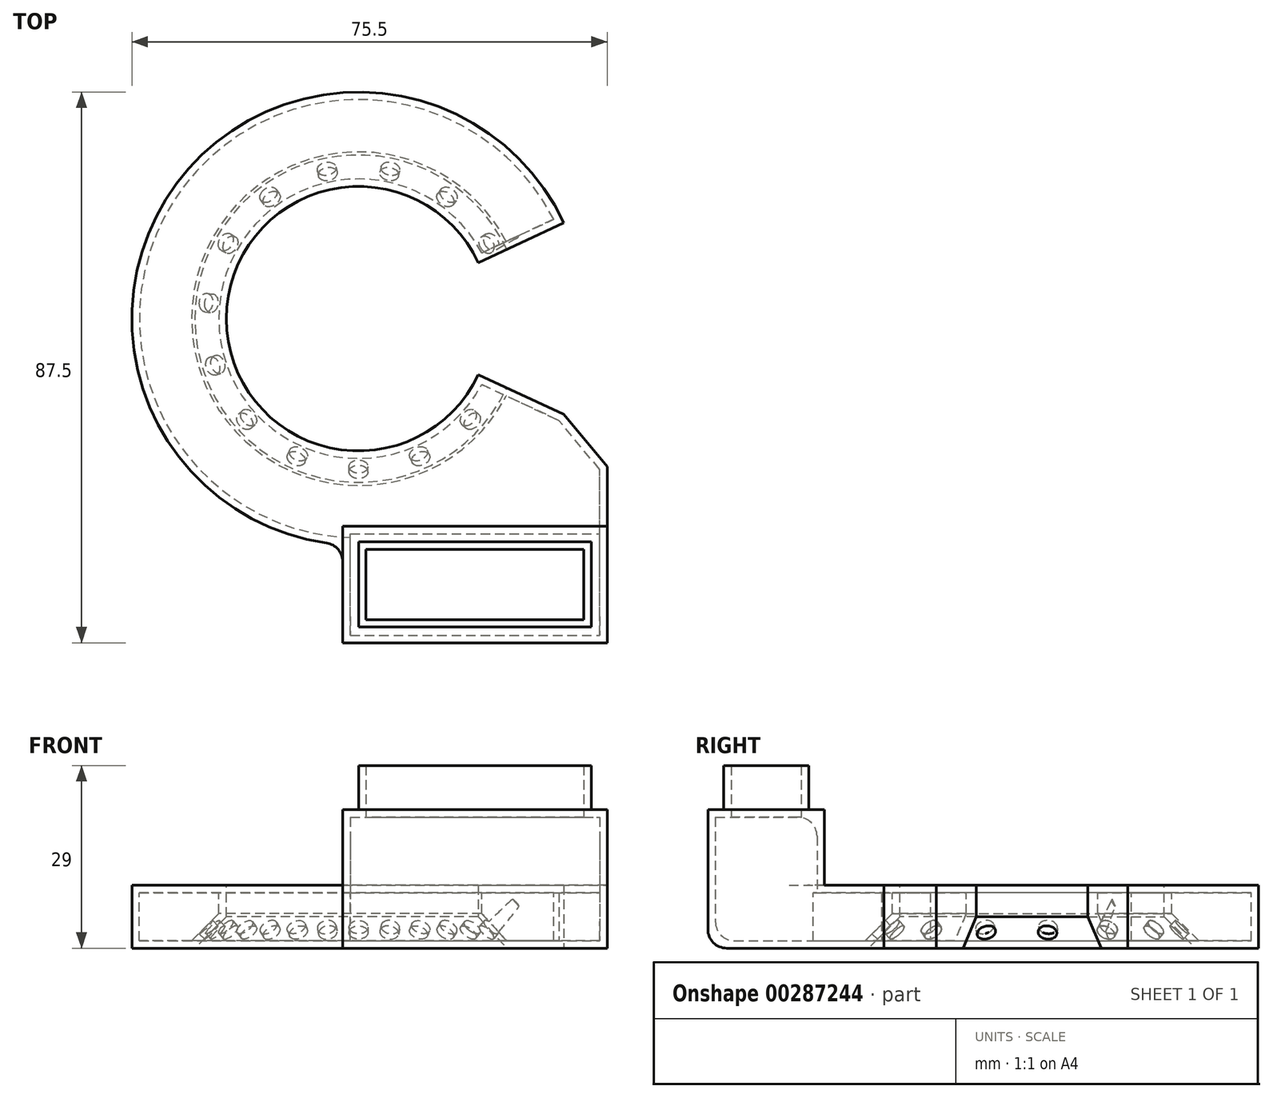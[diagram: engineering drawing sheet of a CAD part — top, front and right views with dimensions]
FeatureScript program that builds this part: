
annotation { "Feature Type Name" : "Feature", "Feature Type Description" : "" }
export const myFeature = defineFeature(function(context is Context, id is Id, definition is map)
    precondition{}
    {
        {
            var Q0;
            Q0=qCreatedBy(makeId("Front.planeOp"),FACE);
            var sketch = newSketch(context, id + "F0", { "sketchPlane" : qUnion([Q0])});
            skLineSegment(sketch, "E0", {"start": v(0, 66.2) * mm, "end": v(0, -56.66) * mm, "construction": true});
            skLineSegment(sketch, "E1", {"start": v(21, 10) * mm, "end": v(36, 10) * mm});
            skLineSegment(sketch, "E2", {"start": v(36, 10) * mm, "end": v(36, 0) * mm});
            skLineSegment(sketch, "E3", {"start": v(36, 0) * mm, "end": v(26, 0) * mm});
            skLineSegment(sketch, "E4", {"start": v(21, 10) * mm, "end": v(21, 5) * mm});
            skLineSegment(sketch, "E5", {"start": v(21, 5) * mm, "end": v(26, 0) * mm});
            skSolve(sketch);
        }
        {
            var Q0;
            Q0=makeQuery(id+"F0.imprint","IMPRINT",FACE,{"disambiguationData":[TD([[makeQuery(id+"F0.imprint","IMPRINT",EDGE,{"derivedFrom":sQuery(id+"F0.wireOp",EDGE,"E1")}),-1.0]])]});
            var Q1;
            Q1=sQuery(id+"F0.wireOp",EDGE,"E0");
            revolve(context, id + "F1", {"entities" : qUnion([Q0]), "axis" : qUnion([Q1]), "revolveType" : RevolveType.TWO_DIRECTIONS, "angle" : 335 * degree, "angleBack" : 25 * degree});
        }
        {
            var Q0;
            Q0=qCreatedBy(makeId("Top.planeOp"),FACE);
            var sketch = newSketch(context, id + "F2", { "sketchPlane" : qUnion([Q0])});
            skLineSegment(sketch, "E6.bottom", {"start": v(-2.5, -51.5) * mm, "end": v(39.5, -51.5) * mm});
            skLineSegment(sketch, "E6.left", {"start": v(-2.5, -51.5) * mm, "end": v(-2.5, -31.44) * mm});
            skLineSegment(sketch, "E6.right", {"start": v(39.5, -51.5) * mm, "end": v(39.5, -23.5) * mm});
            skPoint(sketch, "E7.orphan", {"position": v(23.56, -10.99) * mm});
            skPoint(sketch, "E8.orphan", {"position": v(23.56, 10.99) * mm});
            skPoint(sketch, "E9.0", {"position": v(32.63, -15.21) * mm});
            skLineSegment(sketch, "E10", {"start": v(39.5, -23.5) * mm, "end": v(32.63, -15.21) * mm});
            skLineSegment(sketch, "E11", {"start": v(32.63, -15.21) * mm, "end": v(-2.5, -31.44) * mm});
            skSolve(sketch);
        }
        {
            var Q0;
            Q0=makeQuery(id+"F2.imprint","IMPRINT",FACE,{"disambiguationData":[TD([[makeQuery(id+"F2.imprint","IMPRINT",EDGE,{"derivedFrom":sQuery(id+"F2.wireOp",EDGE,"E6.bottom")}),1.0]])]});
            var Q1;
            Q1=makeQuery(id+"F1.opRevolve","SWEPT_FACE",FACE,{"disambiguationData":[OSD([sQuery(id+"F0.wireOp",EDGE,"E1")])]});
            extrude(context, id + "F3", {"entities" : qUnion([Q0]), "operationType" : NewBodyOperationType.ADD, "endBound" : BoundingType.UP_TO_SURFACE, "endBoundEntityFace" : qUnion([Q1]), "depth" : 25 * mm});
        }
        {
            var Q0;
            Q0=makeQuery(id+"F3.boolean.opBoolean","MERGE",FACE,{"derivedFrom":[makeQuery(id+"F1.opRevolve","SWEPT_FACE",FACE,{"disambiguationData":[OSD([sQuery(id+"F0.wireOp",EDGE,"E1")])]}),makeQuery(id+"F3.opExtrude","CAP_FACE",FACE,{"disambiguationData":[OSD([sQuery(id+"F2.wireOp",EDGE,"E6.bottom"),sQuery(id+"F2.wireOp",EDGE,"E6.left"),sQuery(id+"F2.wireOp",EDGE,"E6.right"),sQuery(id+"F2.wireOp",EDGE,"E10"),sQuery(id+"F2.wireOp",EDGE,"E11")])],"isStart":false})]});
            var sketch = newSketch(context, id + "F4", { "sketchPlane" : qUnion([Q0])});
            skPoint(sketch, "E12.0", {"position": v(-2.5, -51.5) * mm});
            skLineSegment(sketch, "E13.bottom", {"start": v(-2.5, -51.5) * mm, "end": v(39.5, -51.5) * mm});
            skLineSegment(sketch, "E13.top", {"start": v(-2.5, -32.96) * mm, "end": v(39.5, -32.96) * mm});
            skLineSegment(sketch, "E13.left", {"start": v(-2.5, -51.5) * mm, "end": v(-2.5, -32.96) * mm});
            skLineSegment(sketch, "E13.right", {"start": v(39.5, -51.5) * mm, "end": v(39.5, -32.96) * mm});
            skSolve(sketch);
        }
        {
            var Q0;
            Q0=makeQuery(id+"F4.imprint","IMPRINT",FACE,{"disambiguationData":[TD([[makeQuery(id+"F4.imprint","IMPRINT",EDGE,{"derivedFrom":sQuery(id+"F4.wireOp",EDGE,"E13.bottom")}),1.0]])]});
            extrude(context, id + "F5", {"entities" : qUnion([Q0]), "operationType" : NewBodyOperationType.ADD, "depth" : 12 * mm});
        }
        {
            var Q0;
            Q0=makeQuery(id+"F5.opExtrude","CAP_FACE",FACE,{"disambiguationData":[OSD([sQuery(id+"F4.wireOp",EDGE,"E13.bottom"),sQuery(id+"F4.wireOp",EDGE,"E13.top"),sQuery(id+"F4.wireOp",EDGE,"E13.left"),sQuery(id+"F4.wireOp",EDGE,"E13.right")])],"isStart":false});
            var sketch = newSketch(context, id + "F6", { "sketchPlane" : qUnion([Q0])});
            skPoint(sketch, "E14.0", {"position": v(-2.5, -32.96) * mm});
            skPoint(sketch, "E15.0", {"position": v(-2.5, -51.5) * mm});
            skPoint(sketch, "E16.0", {"position": v(39.5, -51.5) * mm});
            skPoint(sketch, "E17.0", {"position": v(39.5, -32.96) * mm});
            skLineSegment(sketch, "E18", {"start": v(-2.5, -32.96) * mm, "end": v(39.5, -51.5) * mm, "construction": true});
            skLineSegment(sketch, "E19", {"start": v(-2.5, -51.5) * mm, "end": v(39.5, -32.96) * mm, "construction": true});
            skLineSegment(sketch, "E20.bottom", {"start": v(37, -35.46) * mm, "end": v(0, -35.46) * mm});
            skLineSegment(sketch, "E20.top", {"start": v(37, -49) * mm, "end": v(0, -49) * mm});
            skLineSegment(sketch, "E20.left", {"start": v(37, -35.46) * mm, "end": v(37, -49) * mm});
            skLineSegment(sketch, "E20.right", {"start": v(0, -35.46) * mm, "end": v(0, -49) * mm});
            skPoint(sketch, "E20.middle", {"position": v(18.5, -42.23) * mm});
            skSolve(sketch);
        }
        {
            var Q0;
            Q0=makeQuery(id+"F6.imprint","IMPRINT",FACE,{"disambiguationData":[TD([[makeQuery(id+"F6.imprint","IMPRINT",EDGE,{"derivedFrom":sQuery(id+"F6.wireOp",EDGE,"E20.bottom")}),1.0]])]});
            extrude(context, id + "F7", {"entities" : qUnion([Q0]), "operationType" : NewBodyOperationType.ADD, "depth" : 7 * mm});
        }
        {
            var Q0;
            Q0=makeQuery(id+"F7.opExtrude","CAP_FACE",FACE,{"disambiguationData":[OSD([sQuery(id+"F6.wireOp",EDGE,"E20.bottom"),sQuery(id+"F6.wireOp",EDGE,"E20.top"),sQuery(id+"F6.wireOp",EDGE,"E20.left"),sQuery(id+"F6.wireOp",EDGE,"E20.right")])],"isStart":false});
            shell(context, id + "F8", {"entities" : qUnion([Q0]), "thickness" : 1.2 * mm});
        }
        {
            var Q0;
            Q0=qCreatedBy(makeId("Top.planeOp"),FACE);
            var sketch = newSketch(context, id + "F9", { "sketchPlane" : qUnion([Q0])});
            skLineSegment(sketch, "E21", {"start": v(71.7, 0) * mm, "end": v(-68.59, 0) * mm});
            skSolve(sketch);
        }
        {
            var Q0;
            Q0=sQuery(id+"F9.wireOp",EDGE,"E21");
            cPlane(context, id + "F10", {"entities" : qUnion([Q0]), "cplaneType" : CPlaneType.LINE_ANGLE, "offset" : 25 * mm, "angle" : 45 * degree, "width" : 150 * mm, "height" : 150 * mm});
        }
        {
            var Q0;
            Q0=qCreatedBy(id+"F10.planeOp",FACE);
            var sketch = newSketch(context, id + "F11", { "sketchPlane" : qUnion([Q0])});
            skCircle(sketch, "E22", {"center": v(0, -14.85) * mm, "radius": 1.5 * mm});
            skSolve(sketch);
        }
        {
            var Q0;
            Q0=makeQuery(id+"F11.imprint","IMPRINT",FACE,{"disambiguationData":[TD([[makeQuery(id+"F11.imprint","IMPRINT",EDGE,{"derivedFrom":sQuery(id+"F11.wireOp",EDGE,"E22")}),1.0]])]});
            extrude(context, id + "F12", {"entities" : qUnion([Q0]), "depth" : 25 * mm});
        }
        {
            var Q0;
            Q0=makeQuery(id+"F12.opExtrude","SWEPT_BODY",BODY,{"disambiguationData":[OSD([sQuery(id+"F11.wireOp",EDGE,"E22")])]});
            var Q1;
            Q1=sQuery(id+"F0.wireOp",EDGE,"E0");
            circularPattern(context, id + "F13", {"operationType" : NewBodyOperationType.REMOVE, "entities" : qUnion([Q0]), "axis" : qUnion([Q1]), "angle" : 360 * degree, "instanceCount" : 15, "equalSpace" : true});
        }
        {
            var Q0;
            Q0=makeQuery(id+"F3.opExtrude","CAP_EDGE",EDGE,{"disambiguationData":[OSD([sQuery(id+"F2.wireOp",EDGE,"E6.bottom")])],"isStart":true});
            var Q1;
            Q1=makeQuery(id+"F8.opShell","OFFSET_EDGE",EDGE,{"disambiguationData":[OSD([sQuery(id+"F2.wireOp",EDGE,"E6.bottom")])]});
            var Q2;
            {var subQ0=sQuery(id+"F4.wireOp",EDGE,"E13.top");Q2=makeQuery(id+"F8.opShell","OFFSET_EDGE",EDGE,{"disambiguationData":[OSD([subQ0]),TDD([makeQuery(id+"F5.opExtrude","CAP_EDGE",EDGE,{"disambiguationData":[OSD([subQ0])],"isStart":true})])]});}
            var Q3;
            Q3=makeQuery(id+"F5.opExtrude","CAP_EDGE",EDGE,{"disambiguationData":[OSD([sQuery(id+"F4.wireOp",EDGE,"E13.top")])],"isStart":true});
            var Q4;
            Q4=makeQuery(id+"F3.boolean.opBoolean","INTERSECT",EDGE,{"derivedFrom":[makeQuery(id+"F1.opRevolve","SWEPT_FACE",FACE,{"disambiguationData":[OSD([sQuery(id+"F0.wireOp",EDGE,"E2")])]}),makeQuery(id+"F3.opExtrude","SWEPT_FACE",FACE,{"disambiguationData":[OSD([sQuery(id+"F2.wireOp",EDGE,"E6.left")])]})]});
            var Q5;
            Q5=makeQuery(id+"F3.boolean.opBoolean","INTERSECT",EDGE,{"derivedFrom":[makeQuery(id+"F1.opRevolve","SWEPT_FACE",FACE,{"disambiguationData":[OSD([sQuery(id+"F0.wireOp",EDGE,"E2")])]}),makeQuery(id+"F3.opExtrude","SWEPT_FACE",FACE,{"disambiguationData":[OSD([sQuery(id+"F2.wireOp",EDGE,"E6.left")])]})]});
            fillet(context, id + "F14", {"entities" : qUnion([Q0, Q1, Q2, Q3, Q4, Q5]), "radius" : 3 * mm, "tangentPropagation" : true, "allowEdgeOverflow" : false});
        }
    });
